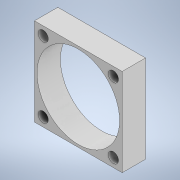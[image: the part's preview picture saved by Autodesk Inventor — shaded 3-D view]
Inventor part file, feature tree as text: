
AUTODESK INVENTOR PART (.ipt)
format: ipt  version: 2022.1 (Build 261234000, 234)  size: 117,248 bytes
history: native  units: mm
features: sketch x1, extrude x1, hole x1
ambient origin geometry x8: Origin, YZ Plane, XZ Plane, XY Plane, X Axis, Y Axis, Z Axis, Center Point
bodies: Solid1 (feature_tree)
feature tree (3):
  sketch  "Sketch1"  dims[d0=30.0mm d1=28.25mm d2=24.0mm d3=8.0mm d4=0.0mm d5=3.5mm d6=6.0mm d7=5.5372mm d8=5.55244mm d9=90.0deg d10=7.1374mm d11=0.0mm]
  extrude  "Extrusion1"  Depth=8.0mm
  hole  "Hole1"  [1 undecoded]
note: 1 required parameter value undecoded (feature->parameter linkage not recoverable at this tier; creation-order binding heuristic only, values carry confidence <= 0.55)
